# Revit family: Hook-DoubleHolder-Vitra-BaseSeries-A44116
name_source: partatom
category: Plumbing Fixtures
revit_build: Autodesk Revit 2017 (Build: 20160225_1515(x64)
units: mm (PartAtom-declared; Revit-internal decimal feet)

## family parameters
Cut with Voids When Loaded = No
Host = Face
OmniClass Number = 23.45.00.00
OmniClass Title = Sanitary, Laundry, and Cleaning Equipment
Part Type = Normal
Room Calculation Point = No
Round Connector Dimension = Use Diameter
Shared = Yes

## types (1)
- Hook-DoubleHolder-Vitra-BaseSeries-A44116
    Article No. (default) = A44116
    BIMobject category = Furniture - Hooks & Hangers
    Brand = VitrA
    CW Connection = No
    Coating Material = Chrome (Metal)
    Color = Chrome
    Default Elevation = 0 mm  [stored 0 ft]
    Description = Base Hook Holder
    Design country = Turkey
    HW Connection = No
    IFC Classification = Sanitary Terminal
    Manufacturer = Vitra
    Manufacturer name = Vitra
    Masterformat 2014 Code = 41 23 19
    Masterformat 2014 Description = Hooks
    Model = A44116
    Mounting type = Wall Mounted
    NBS Referans Code = 35-75-18
    NBS Referans Description = Clothes Hooks
    Nominal Depth (mm) = 50 mm  [stored 0.164042 ft]
    Nominal Height (mm) = 50 mm  [stored 0.164042 ft]
    Nominal Width (mm) = 50 mm  [stored 0.164042 ft]
    OmniClass Code = 23-31 25 27
    OmniClass Description = Robe Hooks
    Product SKU = A44116
    Product Type = Hook Holder
    Product certification = https://www.vitraglobal.com
    Product family = Base Series
    Product group = Hook Holder
    Product url = https://vitraglobal.com
    Technical description = https://vitraglobal.com
    UNSPSC Description = Furniture and Furnishings
    URL = https://vitraglobal.com
    Uniclass 1.4 Code = L41821
    Uniclass 1.4 Description = Fasteners, stays, hooks
    Uniclass 2.0 Code = PR-35-75-18
    Uniclass 2.0 Description = Clothes Hooks
    Uniclass 2015 Code = Pr_40_30_78_15
    Uniclass 2015 Name = Clothes hooks
    Uniformat II Code = E20
    Uniformat II Description = FURNISHINGS
    Vent Connection = No
    Warranty Period (Year) = 5 years
    Waste Connection = No
    Weight Net (kg) = 0.5
    Youtube = https://www.youtube.com

note: [stored X ft] marks values corroborated as IEEE doubles in the binary element streams (Revit-internal decimal feet)

## geometry (parser evidence)
native form markers: Sweep x3
no freeform markers — native parametric forms only
